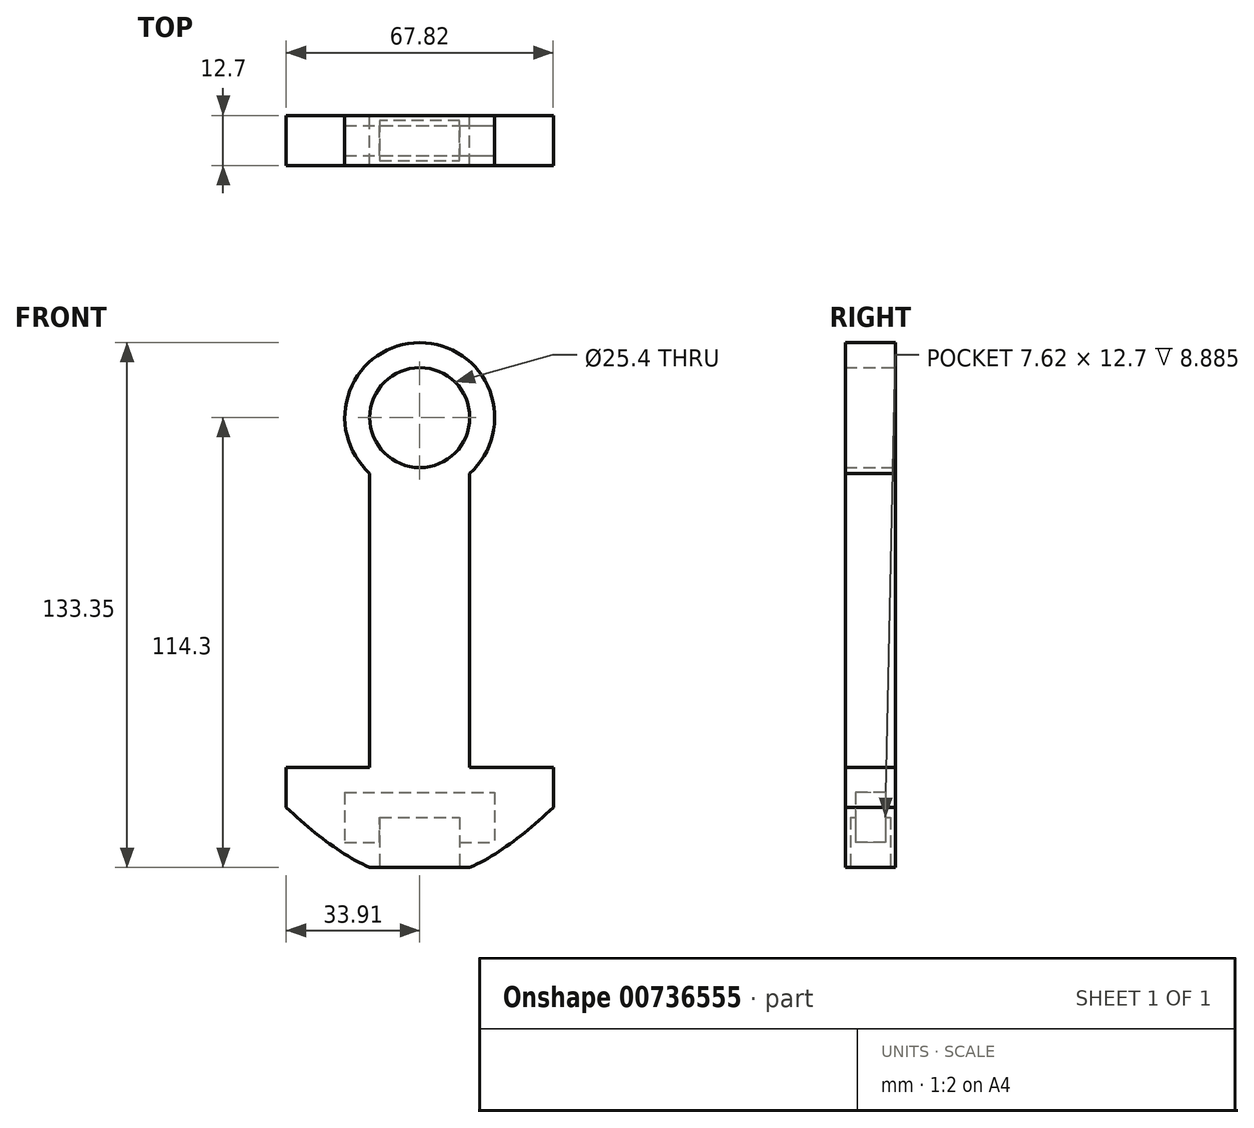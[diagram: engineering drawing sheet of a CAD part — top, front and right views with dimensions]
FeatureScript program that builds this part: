
annotation { "Feature Type Name" : "Feature", "Feature Type Description" : "" }
export const myFeature = defineFeature(function(context is Context, id is Id, definition is map)
    precondition{}
    {
        {
            var Q0;
            Q0=qCreatedBy(makeId("Front.planeOp"),FACE);
            var sketch = newSketch(context, id + "F0", { "sketchPlane" : qUnion([Q0])});
            skLineSegment(sketch, "E0", {"start": v(0, 0) * mm, "end": v(12.7, 0) * mm});
            skLineSegment(sketch, "E1", {"start": v(0, 0) * mm, "end": v(-12.7, 0) * mm});
            skLineSegment(sketch, "E2", {"start": v(-12.7, 0) * mm, "end": v(-12.7, 50.8) * mm});
            skLineSegment(sketch, "E3", {"start": v(-12.7, 50.8) * mm, "end": v(12.7, 50.8) * mm});
            skLineSegment(sketch, "E4", {"start": v(12.7, 50.8) * mm, "end": v(12.7, 0) * mm});
            skLineSegment(sketch, "E5", {"start": v(0, 50.8) * mm, "end": v(0, 63.5) * mm});
            skCircle(sketch, "E6", {"center": v(0, 63.5) * mm, "radius": 12.7 * mm});
            skCircle(sketch, "E7", {"center": v(0, 63.5) * mm, "radius": 19.05 * mm});
            skLineSegment(sketch, "E8", {"start": v(12.7, 0) * mm, "end": v(12.7, -50.8) * mm});
            skLineSegment(sketch, "E9", {"start": v(12.7, -50.8) * mm, "end": v(-12.7, -50.8) * mm});
            skLineSegment(sketch, "E10", {"start": v(-12.7, -50.8) * mm, "end": v(-12.7, 0) * mm});
            skLineSegment(sketch, "E11", {"start": v(0, -25.4) * mm, "end": v(33.91, -25.4) * mm});
            skPoint(sketch, "E11.startSnap0", {"position": v(12.7, -25.4) * mm});
            skLineSegment(sketch, "E12", {"start": v(0, -25.4) * mm, "end": v(-33.91, -25.4) * mm});
            skFitSpline(sketch, "E13", {"points": [v(-44.45, -25.4) * mm, v(-12.7, -50.8) * mm, v(12.7, -50.8) * mm, v(44.45, -25.4) * mm], "startDerivative": vector(88.2, -87.1) * mm, "endDerivative": vector(88.2, 87.1) * mm});
            skLineSegment(sketch, "E14", {"start": v(33.91, -35.8) * mm, "end": v(33.91, -25.4) * mm});
            skLineSegment(sketch, "E15", {"start": v(-33.91, -35.8) * mm, "end": v(-33.91, -25.4) * mm});
            skLineSegment(sketch, "E16", {"start": v(0, 82.55) * mm, "end": v(50.8, 82.55) * mm});
            skLineSegment(sketch, "E17", {"start": v(50.8, 82.55) * mm, "end": v(50.8, -50.8) * mm});
            skLineSegment(sketch, "E18", {"start": v(42.2, 50.8) * mm, "end": v(42.2, -50.8) * mm});
            skLineSegment(sketch, "E19", {"start": v(38.05, -35.58) * mm, "end": v(38.05, 50.8) * mm});
            skPoint(sketch, "E20", {"position": v(0, -53.52) * mm});
            skPoint(sketch, "E20.positionSnap0", {"position": v(0, -50.8) * mm});
            skSolve(sketch);
        }
        {
            var Q0;
            {var subQ5=sQuery(id+"F0.wireOp",EDGE,"E6");Q0=makeQuery(id+"F0.imprint","IMPRINT",FACE,{"disambiguationData":[TD([[makeQuery(id+"F0.imprint","IMPRINT",EDGE,{"derivedFrom":subQ5}),-1.0]])]});}
            var Q1;
            {var subQ1=sQuery(id+"F0.wireOp",EDGE,"E3");var subQ6=sQuery(id+"F0.wireOp",EDGE,"E2");var subQ7=makeQuery(id+"F0.imprint","INTERSECT",VERTEX,{"derivedFrom":[subQ6,subQ1]});Q1=makeQuery(id+"F0.imprint","IMPRINT",FACE,{"disambiguationData":[TD([[makeQuery(id+"F0.imprint","IMPRINT",EDGE,{"disambiguationData":[TD([[subQ7,1.0]])],"derivedFrom":subQ6}),-1.0]])]});}
            var Q2;
            {var subQ1=sQuery(id+"F0.wireOp",EDGE,"E0");Q2=makeQuery(id+"F0.imprint","IMPRINT",FACE,{"disambiguationData":[TD([[makeQuery(id+"F0.imprint","IMPRINT",EDGE,{"derivedFrom":subQ1}),1.0]])]});}
            var Q3;
            Q3=makeQuery(id+"F0.imprint","IMPRINT",FACE,{"disambiguationData":[TD([[makeQuery(id+"F0.imprint","IMPRINT",EDGE,{"derivedFrom":sQuery(id+"F0.wireOp",EDGE,"E0")}),-1.0]])]});
            var Q4;
            {var subQ0=sQuery(id+"F0.wireOp",EDGE,"E13");var subQ3=sQuery(id+"F0.wireOp",EDGE,"E12");var subQ5=makeQuery(id+"F0.imprint","INTERSECT",VERTEX,{"derivedFrom":[subQ3,subQ0]});Q4=makeQuery(id+"F0.imprint","IMPRINT",FACE,{"disambiguationData":[TD([[makeQuery(id+"F0.imprint","IMPRINT",EDGE,{"disambiguationData":[TD([[subQ5,1.0]])],"derivedFrom":subQ3}),1.0]])]});}
            var Q5;
            {var subQ7=sQuery(id+"F0.wireOp",EDGE,"E9");Q5=makeQuery(id+"F0.imprint","IMPRINT",FACE,{"disambiguationData":[TD([[makeQuery(id+"F0.imprint","IMPRINT",EDGE,{"derivedFrom":subQ7}),-1.0]])]});}
            var Q6;
            {var subQ0=sQuery(id+"F0.wireOp",EDGE,"E13");var subQ3=sQuery(id+"F0.wireOp",EDGE,"E11");var subQ5=makeQuery(id+"F0.imprint","INTERSECT",VERTEX,{"derivedFrom":[subQ3,subQ0]});Q6=makeQuery(id+"F0.imprint","IMPRINT",FACE,{"disambiguationData":[TD([[makeQuery(id+"F0.imprint","IMPRINT",EDGE,{"disambiguationData":[TD([[subQ5,1.0]])],"derivedFrom":subQ3}),-1.0]])]});}
            extrude(context, id + "F1", {"entities" : qUnion([Q0, Q1, Q2, Q3, Q4, Q5, Q6]), "depth" : 12.7 * mm, "offsetDistance" : 25.4 * mm});
        }
        {
            var Q0;
            Q0=qCreatedBy(makeId("Right.planeOp"),FACE);
            var sketch = newSketch(context, id + "F2", { "sketchPlane" : qUnion([Q0])});
            skLineSegment(sketch, "E21", {"start": v(0, 0) * mm, "end": v(0, -50.8) * mm});
            skLineSegment(sketch, "E22", {"start": v(0, -45.01) * mm, "end": v(0, -31.75) * mm});
            skLineSegment(sketch, "E23", {"start": v(-10.16, -31.75) * mm, "end": v(-10.16, -44.45) * mm});
            skLineSegment(sketch, "E24", {"start": v(-5.08, -31.75) * mm, "end": v(0, -31.75) * mm});
            skLineSegment(sketch, "E25", {"start": v(-5.08, -31.75) * mm, "end": v(-10.16, -31.75) * mm});
            skLineSegment(sketch, "E26", {"start": v(-5.08, -44.45) * mm, "end": v(-10.16, -44.45) * mm});
            skPoint(sketch, "E27.orphan", {"position": v(-10.16, -38.1) * mm});
            skPoint(sketch, "E28.orphan", {"position": v(0, -38.1) * mm});
            skPoint(sketch, "E29.end.orphan", {"position": v(-10.16, -25.4) * mm});
            skPoint(sketch, "E29.start.orphan", {"position": v(0, -25.4) * mm});
            skPoint(sketch, "E30.orphan", {"position": v(-10.16, -50.8) * mm});
            skLineSegment(sketch, "E31", {"start": v(0, -31.75) * mm, "end": v(-2.54, -31.75) * mm});
            skLineSegment(sketch, "E32", {"start": v(-10.16, -31.75) * mm, "end": v(-7.62, -31.75) * mm});
            skPoint(sketch, "E33.end.orphan", {"position": v(-2.54, -44.73) * mm});
            skLineSegment(sketch, "E34", {"start": v(-2.54, -31.75) * mm, "end": v(-2.54, -44.45) * mm});
            skLineSegment(sketch, "E35", {"start": v(-2.54, -44.45) * mm, "end": v(-5.08, -44.45) * mm});
            skLineSegment(sketch, "E36", {"start": v(-10.16, -31.75) * mm, "end": v(-12.7, -31.75) * mm});
            skPoint(sketch, "E37.end.orphan", {"position": v(-7.62, -44.45) * mm});
            skSolve(sketch);
        }
        {
            var Q0;
            Q0 = qSketchRegion(id + "F2", true);
            extrude(context, id + "F3", {"entities" : qUnion([Q0]), "operationType" : NewBodyOperationType.REMOVE, "oppositeDirection" : true, "depth" : 19.05 * mm, "offsetDistance" : 25.4 * mm, "hasSecondDirection" : true, "secondDirectionOppositeDirection" : false, "secondDirectionDepth" : 19.05 * mm});
        }
        {
            var Q0;
            Q0=makeQuery(id+"F1.opExtrude","SWEPT_FACE",FACE,{"disambiguationData":[OSD([sQuery(id+"F0.wireOp",EDGE,"E9")])]});
            var sketch = newSketch(context, id + "F4", { "sketchPlane" : qUnion([Q0])});
            skLineSegment(sketch, "E38", {"start": v(0, 0) * mm, "end": v(0, 1.27) * mm});
            skLineSegment(sketch, "E39", {"start": v(0, 1.27) * mm, "end": v(10.16, 1.27) * mm});
            skLineSegment(sketch, "E40", {"start": v(0, 12.7) * mm, "end": v(0, 11.43) * mm});
            skLineSegment(sketch, "E41", {"start": v(0, 11.43) * mm, "end": v(10.16, 11.43) * mm});
            skLineSegment(sketch, "E42", {"start": v(10.16, 11.43) * mm, "end": v(10.16, 1.27) * mm});
            skLineSegment(sketch, "E43", {"start": v(0, 1.27) * mm, "end": v(-10.17, 1.27) * mm});
            skLineSegment(sketch, "E44", {"start": v(-10.17, 1.27) * mm, "end": v(-10.17, 11.43) * mm});
            skLineSegment(sketch, "E45", {"start": v(-10.17, 11.43) * mm, "end": v(0, 11.43) * mm});
            skLineSegment(sketch, "E46.trimOffspring", {"start": v(0, 11.43) * mm, "end": v(0, 12.7) * mm});
            skSolve(sketch);
        }
        {
            var Q0;
            Q0=makeQuery(id+"F4.imprint","IMPRINT",FACE,{"disambiguationData":[TD([[makeQuery(id+"F4.imprint","IMPRINT",EDGE,{"derivedFrom":sQuery(id+"F4.wireOp",EDGE,"E39")}),1.0]])]});
            extrude(context, id + "F5", {"entities" : qUnion([Q0]), "operationType" : NewBodyOperationType.REMOVE, "oppositeDirection" : true, "depth" : 12.7 * mm, "offsetDistance" : 25.4 * mm});
        }
    });
